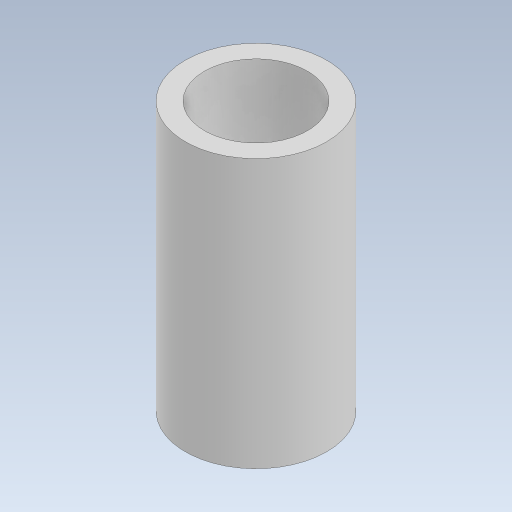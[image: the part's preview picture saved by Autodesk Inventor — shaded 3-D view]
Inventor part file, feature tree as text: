
AUTODESK INVENTOR PART (.ipt)
format: ipt  version: 2023.5 (Build 275446000, 446)  size: 90,112 bytes
history: native  units: mm
features: extrude x1, sketch x1
ambient origin geometry x8: Origin, YZ Plane, XZ Plane, XY Plane, X Axis, Y Axis, Z Axis, Center Point
bodies: Solid1 (feature_tree)
feature tree (2):
  extrude  "Extrusion1"  Depth=10.0mm
  sketch  "Sketch1"  dims[d0=7.3mm d1=10.0mm d2=19.0mm d3=0.0mm]
